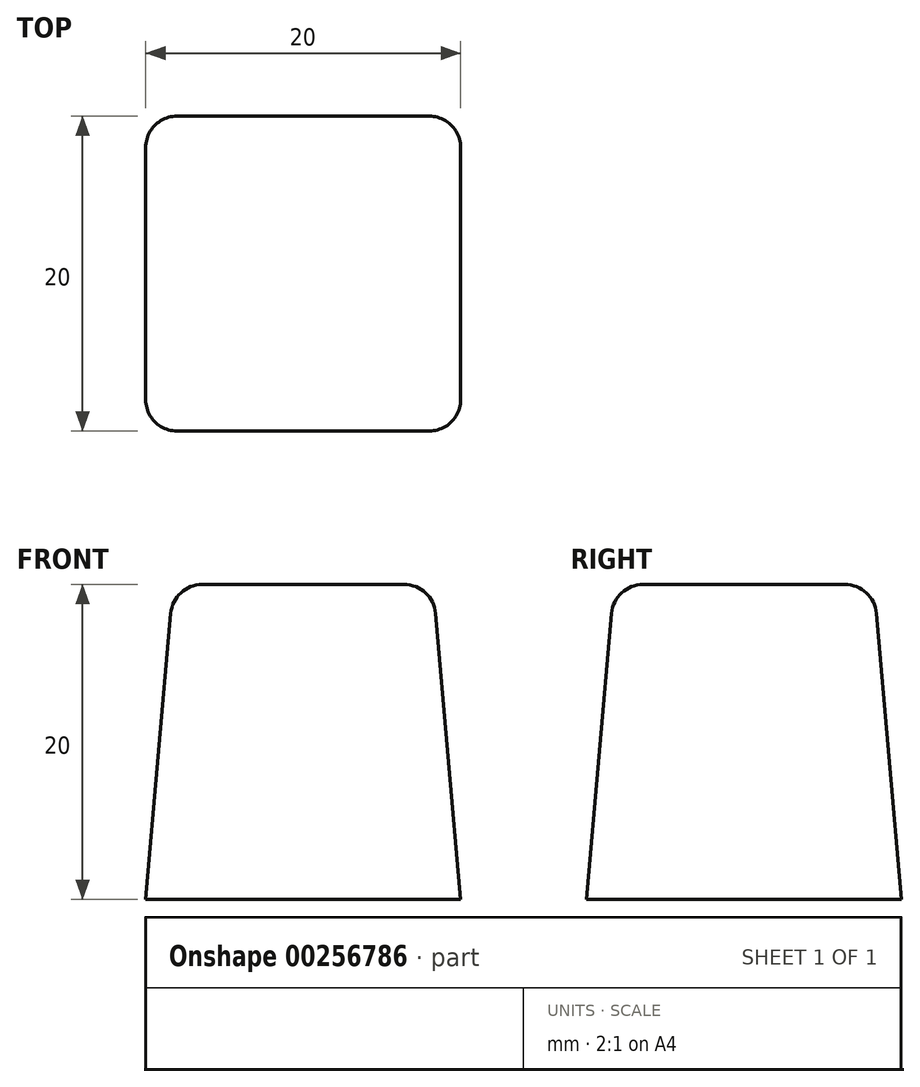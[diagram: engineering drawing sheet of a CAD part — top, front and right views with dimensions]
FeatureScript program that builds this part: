
annotation { "Feature Type Name" : "Feature", "Feature Type Description" : "" }
export const myFeature = defineFeature(function(context is Context, id is Id, definition is map)
    precondition{}
    {
        {
            var Q0;
            Q0=qCreatedBy(makeId("Top.planeOp"),FACE);
            var sketch = newSketch(context, id + "F0", { "sketchPlane" : qUnion([Q0])});
            skLineSegment(sketch, "E0.bottom", {"start": v(10, -10) * mm, "end": v(-10, -10) * mm});
            skLineSegment(sketch, "E0.top", {"start": v(10, 10) * mm, "end": v(-10, 10) * mm});
            skLineSegment(sketch, "E0.left", {"start": v(10, -10) * mm, "end": v(10, 10) * mm});
            skLineSegment(sketch, "E0.right", {"start": v(-10, -10) * mm, "end": v(-10, 10) * mm});
            skPoint(sketch, "E0.middle", {"position": v(0, 0) * mm});
            skSolve(sketch);
        }
        {
            var Q0;
            Q0 = qSketchRegion(id + "F0", true);
            extrude(context, id + "F1", {"entities" : qUnion([Q0]), "depth" : 20 * mm, "hasDraft" : true, "draftAngle" : 5 * degree, "draftPullDirection" : true});
        }
        {
            var Q0;
            Q0=makeQuery(id+"F1.opExtrude","CAP_EDGE",EDGE,{"disambiguationData":[OSD([sQuery(id+"F0.wireOp",EDGE,"E0.top")])],"isStart":false});
            var Q1;
            Q1=makeQuery(id+"F1.opExtrude","CAP_EDGE",EDGE,{"disambiguationData":[OSD([sQuery(id+"F0.wireOp",EDGE,"E0.right")])],"isStart":false});
            var Q2;
            Q2=makeQuery(id+"F1.opExtrude","CAP_FACE",FACE,{"disambiguationData":[OSD([sQuery(id+"F0.wireOp",EDGE,"E0.bottom"),sQuery(id+"F0.wireOp",EDGE,"E0.top"),sQuery(id+"F0.wireOp",EDGE,"E0.left"),sQuery(id+"F0.wireOp",EDGE,"E0.right")])],"isStart":false});
            var Q3;
            Q3=makeQuery(id+"F1.opExtrude","SWEPT_EDGE",EDGE,{"disambiguationData":[OSD([sQuery(id+"F0.wireOp",EDGE,"E0.top"),sQuery(id+"F0.wireOp",EDGE,"E0.left")])]});
            var Q4;
            Q4=makeQuery(id+"F1.opExtrude","SWEPT_EDGE",EDGE,{"disambiguationData":[OSD([sQuery(id+"F0.wireOp",EDGE,"E0.top"),sQuery(id+"F0.wireOp",EDGE,"E0.right")])]});
            var Q5;
            Q5=makeQuery(id+"F1.opExtrude","SWEPT_EDGE",EDGE,{"disambiguationData":[OSD([sQuery(id+"F0.wireOp",EDGE,"E0.bottom"),sQuery(id+"F0.wireOp",EDGE,"E0.right")])]});
            var Q6;
            Q6=makeQuery(id+"F1.opExtrude","SWEPT_EDGE",EDGE,{"disambiguationData":[OSD([sQuery(id+"F0.wireOp",EDGE,"E0.bottom"),sQuery(id+"F0.wireOp",EDGE,"E0.left")])]});
            fillet(context, id + "F2", {"entities" : qUnion([Q0, Q1, Q2, Q3, Q4, Q5, Q6]), "radius" : 2 * mm, "tangentPropagation" : true, "allowEdgeOverflow" : false});
        }
    });
